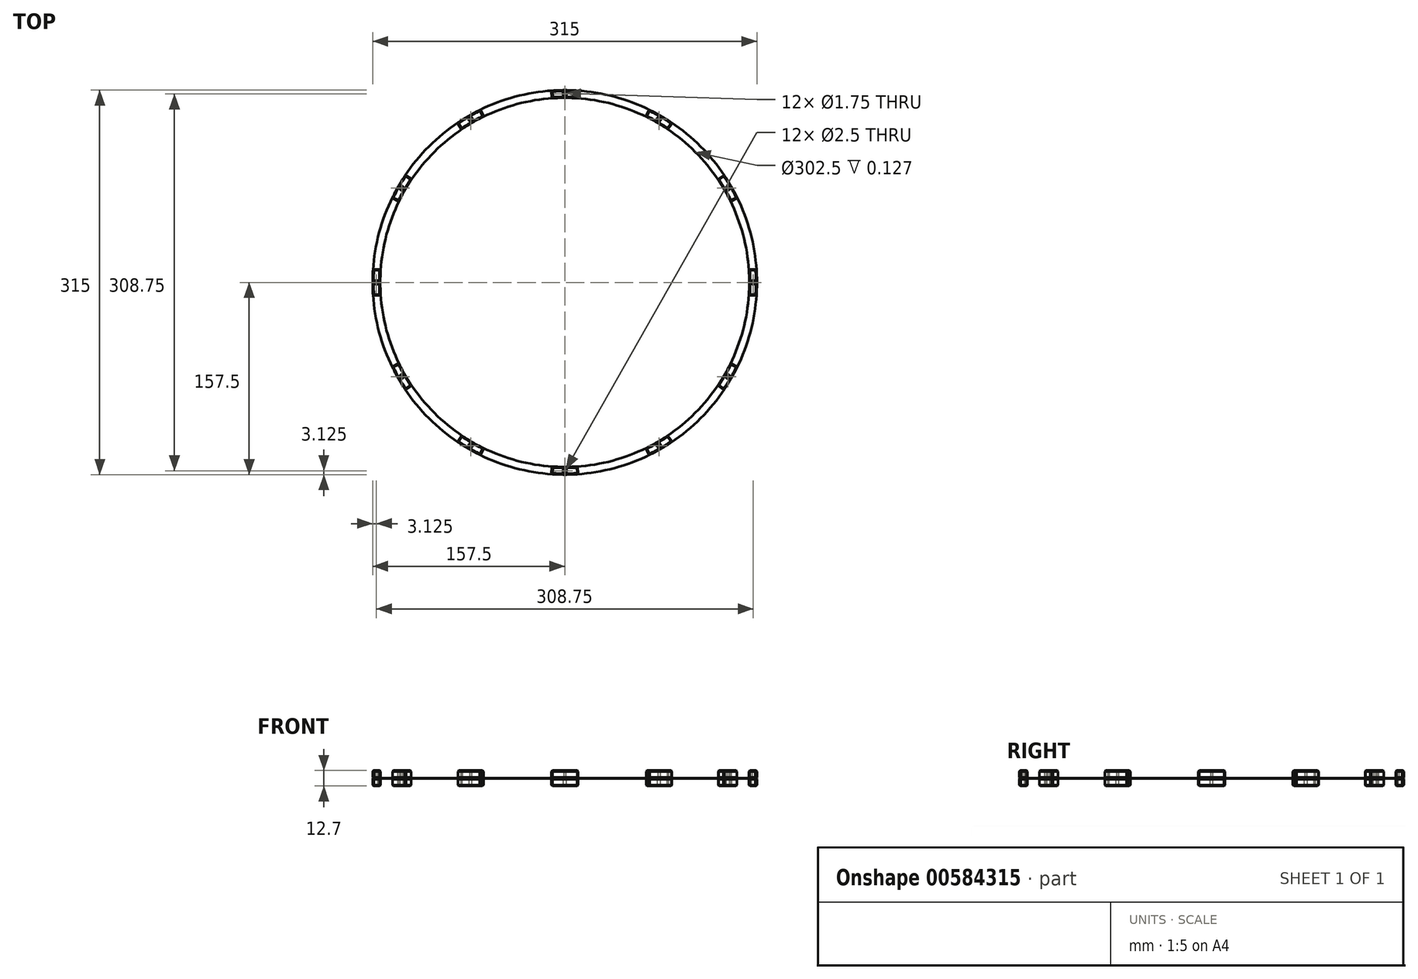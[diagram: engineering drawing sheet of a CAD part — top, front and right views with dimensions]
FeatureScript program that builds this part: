
annotation { "Feature Type Name" : "Feature", "Feature Type Description" : "" }
export const myFeature = defineFeature(function(context is Context, id is Id, definition is map)
    precondition{}
    {
        {
            var Q0;
            Q0=qCreatedBy(makeId("Top.planeOp"),FACE);
            var sketch = newSketch(context, id + "F0", { "sketchPlane" : qUnion([Q0])});
            skCircle(sketch, "E0", {"center": v(0, 0) * mm, "radius": 151.25 * mm});
            skCircle(sketch, "E1", {"center": v(0, 0) * mm, "radius": 157.5 * mm});
            skSolve(sketch);
        }
        {
            var Q0;
            Q0 = qSketchRegion(id + "F0", true);
            extrude(context, id + "F1", {"entities" : qUnion([Q0]), "endBound" : BoundingType.SYMMETRIC, "depth" : 0.13 * mm, "offsetDistance" : 25.4 * mm});
        }
        {
            var Q0;
            Q0=qCreatedBy(makeId("Top.planeOp"),FACE);
            var sketch = newSketch(context, id + "F2", { "sketchPlane" : qUnion([Q0])});
            skLineSegment(sketch, "E2", {"start": v(0, 157.5) * mm, "end": v(0, 151.25) * mm, "construction": true});
            skCircle(sketch, "E3", {"center": v(0, 154.37) * mm, "radius": 0.88 * mm});
            skCircle(sketch, "E4", {"center": v(0, 154.37) * mm, "radius": 1.25 * mm});
            skLineSegment(sketch, "E5", {"start": v(10.99, 157.12) * mm, "end": v(10.55, 150.88) * mm});
            skLineSegment(sketch, "E6", {"start": v(10.55, 150.88) * mm, "end": v(0, 0) * mm, "construction": true});
            skArc(sketch, "E7.0", {"start": v(10.99, 157.12) * mm, "mid": v(0, 157.5) * mm, "end": v(-10.99, 157.12) * mm});
            skArc(sketch, "E7.1", {"start": v(10.55, 150.88) * mm, "mid": v(0, 151.25) * mm, "end": v(-10.55, 150.88) * mm});
            skLineSegment(sketch, "E8", {"start": v(0, 0) * mm, "end": v(0, 235.4) * mm, "construction": true});
            skLineSegment(sketch, "E9.MirrorCS", {"start": v(-10.99, 157.12) * mm, "end": v(-10.55, 150.88) * mm});
            skSolve(sketch);
        }
        {
            var Q0;
            Q0=makeQuery(id+"F2.imprint","IMPRINT",FACE,{"disambiguationData":[TD([[makeQuery(id+"F2.imprint","IMPRINT",EDGE,{"derivedFrom":sQuery(id+"F2.wireOp",EDGE,"E4")}),-1.0]])]});
            var Q1;
            Q1=makeQuery(id+"F2.imprint","IMPRINT",FACE,{"disambiguationData":[TD([[makeQuery(id+"F2.imprint","IMPRINT",EDGE,{"derivedFrom":sQuery(id+"F2.wireOp",EDGE,"E3")}),-1.0]])]});
            extrude(context, id + "F3", {"entities" : qUnion([Q0, Q1]), "depth" : 6.35 * mm, "offsetDistance" : 25.4 * mm});
        }
        {
            var Q0;
            Q0=makeQuery(id+"F2.imprint","IMPRINT",FACE,{"disambiguationData":[TD([[makeQuery(id+"F2.imprint","IMPRINT",EDGE,{"derivedFrom":sQuery(id+"F2.wireOp",EDGE,"E4")}),-1.0]])]});
            extrude(context, id + "F4", {"entities" : qUnion([Q0]), "oppositeDirection" : true, "depth" : 6.35 * mm, "offsetDistance" : 25.4 * mm});
        }
        {
            var Q0;
            Q0=makeQuery(id+"F4.opExtrude","CAP_FACE",FACE,{"disambiguationData":[OSD([sQuery(id+"F2.wireOp",EDGE,"E4"),sQuery(id+"F2.wireOp",EDGE,"E5"),sQuery(id+"F2.wireOp",EDGE,"E7.0"),sQuery(id+"F2.wireOp",EDGE,"E7.1"),sQuery(id+"F2.wireOp",EDGE,"E9.MirrorCS")])],"isStart":false});
            var Q1;
            Q1=makeQuery(id+"F4.opExtrude","CAP_FACE",FACE,{"disambiguationData":[OSD([sQuery(id+"F2.wireOp",EDGE,"E4"),sQuery(id+"F2.wireOp",EDGE,"E5"),sQuery(id+"F2.wireOp",EDGE,"E7.0"),sQuery(id+"F2.wireOp",EDGE,"E7.1"),sQuery(id+"F2.wireOp",EDGE,"E9.MirrorCS")])],"isStart":true});
            var Q2;
            Q2=makeQuery(id+"F4.opExtrude","SWEPT_FACE",FACE,{"disambiguationData":[OSD([sQuery(id+"F2.wireOp",EDGE,"E7.1")])]});
            var Q3;
            Q3=makeQuery(id+"F4.opExtrude","SWEPT_FACE",FACE,{"disambiguationData":[OSD([sQuery(id+"F2.wireOp",EDGE,"E5")])]});
            var Q4;
            Q4=makeQuery(id+"F4.opExtrude","SWEPT_FACE",FACE,{"disambiguationData":[OSD([sQuery(id+"F2.wireOp",EDGE,"E7.0")])]});
            var Q5;
            Q5=makeQuery(id+"F4.opExtrude","SWEPT_FACE",FACE,{"disambiguationData":[OSD([sQuery(id+"F2.wireOp",EDGE,"E9.MirrorCS")])]});
            var Q6;
            Q6=makeQuery(id+"F3.opExtrude","CAP_FACE",FACE,{"disambiguationData":[OSD([sQuery(id+"F2.wireOp",EDGE,"E3"),sQuery(id+"F2.wireOp",EDGE,"E5"),sQuery(id+"F2.wireOp",EDGE,"E7.0"),sQuery(id+"F2.wireOp",EDGE,"E7.1"),sQuery(id+"F2.wireOp",EDGE,"E9.MirrorCS")])],"isStart":false});
            var Q7;
            Q7=makeQuery(id+"F3.opExtrude","SWEPT_FACE",FACE,{"disambiguationData":[OSD([sQuery(id+"F2.wireOp",EDGE,"E7.1")])]});
            var Q8;
            Q8=makeQuery(id+"F3.opExtrude","SWEPT_FACE",FACE,{"disambiguationData":[OSD([sQuery(id+"F2.wireOp",EDGE,"E5")])]});
            var Q9;
            Q9=makeQuery(id+"F3.opExtrude","SWEPT_FACE",FACE,{"disambiguationData":[OSD([sQuery(id+"F2.wireOp",EDGE,"E9.MirrorCS")])]});
            var Q10;
            Q10=makeQuery(id+"F3.opExtrude","SWEPT_FACE",FACE,{"disambiguationData":[OSD([sQuery(id+"F2.wireOp",EDGE,"E7.0")])]});
            var Q11;
            Q11=makeQuery(id+"F3.opExtrude","CAP_FACE",FACE,{"disambiguationData":[OSD([sQuery(id+"F2.wireOp",EDGE,"E3"),sQuery(id+"F2.wireOp",EDGE,"E5"),sQuery(id+"F2.wireOp",EDGE,"E7.0"),sQuery(id+"F2.wireOp",EDGE,"E7.1"),sQuery(id+"F2.wireOp",EDGE,"E9.MirrorCS")])],"isStart":true});
            chamfer(context, id + "F5", {"entities" : qUnion([Q0, Q1, Q2, Q3, Q4, Q5, Q6, Q7, Q8, Q9, Q10, Q11]), "width" : 0.8 * mm, "tangentPropagation" : true});
        }
        {
            var Q0;
            Q0=makeQuery(id+"F3.opExtrude","SWEPT_BODY",BODY,{"disambiguationData":[OSD([sQuery(id+"F2.wireOp",EDGE,"E3"),sQuery(id+"F2.wireOp",EDGE,"E5"),sQuery(id+"F2.wireOp",EDGE,"E7.0"),sQuery(id+"F2.wireOp",EDGE,"E7.1"),sQuery(id+"F2.wireOp",EDGE,"E9.MirrorCS")])]});
            var Q1;
            Q1=makeQuery(id+"F4.opExtrude","SWEPT_BODY",BODY,{"disambiguationData":[OSD([sQuery(id+"F2.wireOp",EDGE,"E4"),sQuery(id+"F2.wireOp",EDGE,"E5"),sQuery(id+"F2.wireOp",EDGE,"E7.0"),sQuery(id+"F2.wireOp",EDGE,"E7.1"),sQuery(id+"F2.wireOp",EDGE,"E9.MirrorCS")])]});
            var Q2;
            Q2=makeQuery(id+"F1.opExtrude","CAP_EDGE",EDGE,{"disambiguationData":[OSD([sQuery(id+"F0.wireOp",EDGE,"E0")])],"isStart":false});
            circularPattern(context, id + "F6", {"entities" : qUnion([Q0, Q1]), "axis" : qUnion([Q2]), "angle" : 360 * degree, "instanceCount" : 12, "equalSpace" : true});
        }
    });
